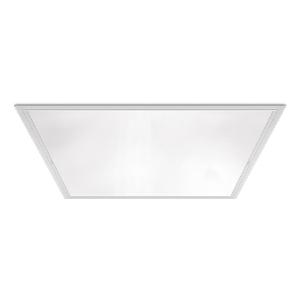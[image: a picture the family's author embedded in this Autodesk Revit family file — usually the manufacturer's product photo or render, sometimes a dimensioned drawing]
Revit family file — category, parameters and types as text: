
# Revit family: 3f_filippi_-_l_340_luce_diffusa_lgs_ip65v_3f_filippi_-_24001_-_l_340_45w-940_dali_lgs_ip65v_596x596
name_source: partatom
category: Lighting Fixtures
units: mm (PartAtom-declared; Revit-internal decimal feet)

## family parameters
Cut with Voids When Loaded = No
Host = Face
Light Source = No
Part Type = Normal
Room Calculation Point = No
Round Connector Dimension = Use Diameter
Shared = No

## types (1)
- 3F Filippi - L 340 Luce Diffusa LGS IP65V (1 x LED, 5066 lm, 52 W, 4000 K)
    Apparent Load = 52 VA
    Approval mark = ENEC
    CIE Flux Codes = 67 92 98 100 100
    Color Rendering = 90
    Color Temperature = 4000 K
    Control Gear = Electronic transformer
    Default Elevation = 1800 mm
    Description = ILLUMINOTECHNICAL
Luminous efficiency 100% (DLOR 100%, ULOR 0%).
Initial luminous flux of the luminaire 5066 lm.
Direct symmetric distribution.
Installation Interdistance Transv.D = 1.19 x hu - Long.D = 1.17 x hu.
Average luminance <3000 cd/m² for radial angles >65°.
Tabular UGR (CIE 117 - 4H-8H; S=0.25H; 70/50/20): RUG 17.4 - 17.5.
Beam angle: 87° - 86°.
Luminous efficacy 97 lm/W.
Lifetime (L93/B10): 30000 h. (tq+25°C)
Lifetime (L90/B10): 50000 h. (tq+25°C)
Lifetime (L85/B10): 80000 h. (tq+25°C)
Lifetime (L80/B10): 100000 h. (tq+25°C)
Sudden decreased luminous flux after 50000 hours: 0% (C0).
Photobiological safety in compliance with IEC/TR 62778: RG0 risk exempt, (IEC 62471).
In compliance with IEC/EN 62722-2-1 - IEC/EN 62717 standards.

SOURCE
Squared LED module 45W/940.
Energy efficiency class (UE 2019/2020 - UE 2019/2015): D.
CIE 13.3 Colour rendering index: CRI >90 (R9 >50%).
IES TM-30 Fidelity Index: Rf = 92 Rg = 101.
CCT nominal colour temperature 4000 K.
Colour initial tolerance (MacAdam): SDCM 3.

MECHANICAL
Housing in hot-galvanised steel, painted in white polyester.
Perimetral frame in white polycarbonate.
LGS micro-prismatic flat diffuser in transparent methacrylate (PMMA), multi-lenticular exterior, anti-glare.
Anti-glare opal polycarbonate filter for brightness uniformity.
Luminaire with limited surface temperature. - D - (EN 60598-2-24)
Dimensions: 596x596 mm, height 80 mm. Weight 4.45 kg.
IP65 protection degree for exposed part, IP40 for recessed part.
Mechanical strength to impacts IK06 (1 joule).
Glow-wire test resistance 650°C.

ELECTRICAL
Wiring on a separate unit.
Halogen Free DALI-2 DATI (Parts 251, 252, 253), PUSH-DIM, electronic wiring 230V-50/60Hz, power factor 0.95 at full load, THD <25%, constant output current, SELV, class II, 1 driver, 1 DALI addresse.
Power of the luminaire 52 W.
CE - IEC 60598-1 - EN 60598-1.
SAFE FLICKER: PstLM=<1 and SVM=<0.4 (IEC TR 61547-1 and IEC TR 63158), to ensure a more comfortable and safe light.
Luminaire compliant with EN 60598-2-22 for power supply from a centralised emergency system CPSS (Central Power Supply System), not incorporated in the luminaire - high risk areas excluded. The default power and flux are 100% in AC and 15% in DC.
Ambient temperature from 0°C to +40°C.
Temperature class T6 max 85°C.
Relative humidity UR: <85%.

INSTALLATION
Lay-on or pull-up recessed fitting using frame accessory.
All accessories dedicated to this product are available on the Catalog and on our website www.3F-Filippi.com.

APPLICATIONS
Suitable product for food production plants (HACCP), IFS (Food Version 6), BRC (GSFS Food Version 7).
In environments requiring protection and simplified cleaning.
Hospitals, pharmaceutical, chemical, aseptic laboratories, sterilised rooms.
Environments: with VDTs, meeting rooms, offices.
Environments: architectural, commercial, staterooms, banks.
Environments where demanding visual tasks are performed and soft diffuse light is required for optimal visual comfort and total shielding of the light source.

LIGHT MANAGEMENT
Recommended minimum setting: 10%.
The luminaire, equipped with (DALI-2 DATI) driver, can be controlled manually with 3F Easy Dim technology or automatically/manually with wired or wireless DALI/D2D control systems.
The D2D driver guarantees interoperability with other devices with the same certification by making the following information available:
Device Data (Part 251), Energy Report (Part 252), Diagnosis & Maintenance (Part 253).
In electrical systems without a regulation system (manual or automatic) and DALI bus, a suitable jumper must be made on the DA-DA terminals of the appliance.

WARNING
Luminaire designed for disposal/recycling at end-of-life.
Replaceable (LED only) light source by a professional. Replaceable control gear by a professional.
    Height = 0 mm  [stored 0 ft]
    Lamp = 1 x LED
    Lamp Light Flux = 5066 lm
    Lamp Power = 52 W
    Lamp count = 1
    Length = 596 mm
    Lifetime = 50000 h
    Luminous efficacy = 97 lm/W
    Manufacturer = 3F Filippi
    ModVariant = No
    Model = 3F Filippi - 24001 - L 340 45W-940 DALI LGS IP65V 596x596
    Mounting Place = Ceiling
    Mounting Type = Recessed
    Number of Poles = 1
    OnlyDefault = Yes
    Power Factor = 1
    Product Name = 3F Filippi - L 340 Luce Diffusa LGS IP65V
    Product group = recessed luminaire
    ProductGroupID = 4
    Protection Class = Protection class II
    Protection Degree = IP 40
    RLX_Detail_Level = 1
    RLX_Emergency_Light_Flux = 0 lm
    RLX_Emergency_Type = 0
    RLX_Emergency_Type_DB = No
    RlxData = <blob elided: 156445 chars, md5=b0711bde>
    Socket = socket
    Standby Power = 0 W
    System Light Flux = 5066 lm
    System Power = 52 W
    Type Comments = Product without accessories
    Type Image = 3ffilippi_l_340_luce_diffusa_lgs_ip65v.jpg
    URL = http://relux.com
    VarID = ---
    Voltage = 0 V
    Weight = 0.00 kg
    Width = 596 mm

note: [stored X ft] marks values corroborated as IEEE doubles in the binary element streams (Revit-internal decimal feet)

## geometry (parser evidence)
native form markers: Blend x4, Sweep x10
no freeform markers — native parametric forms only
